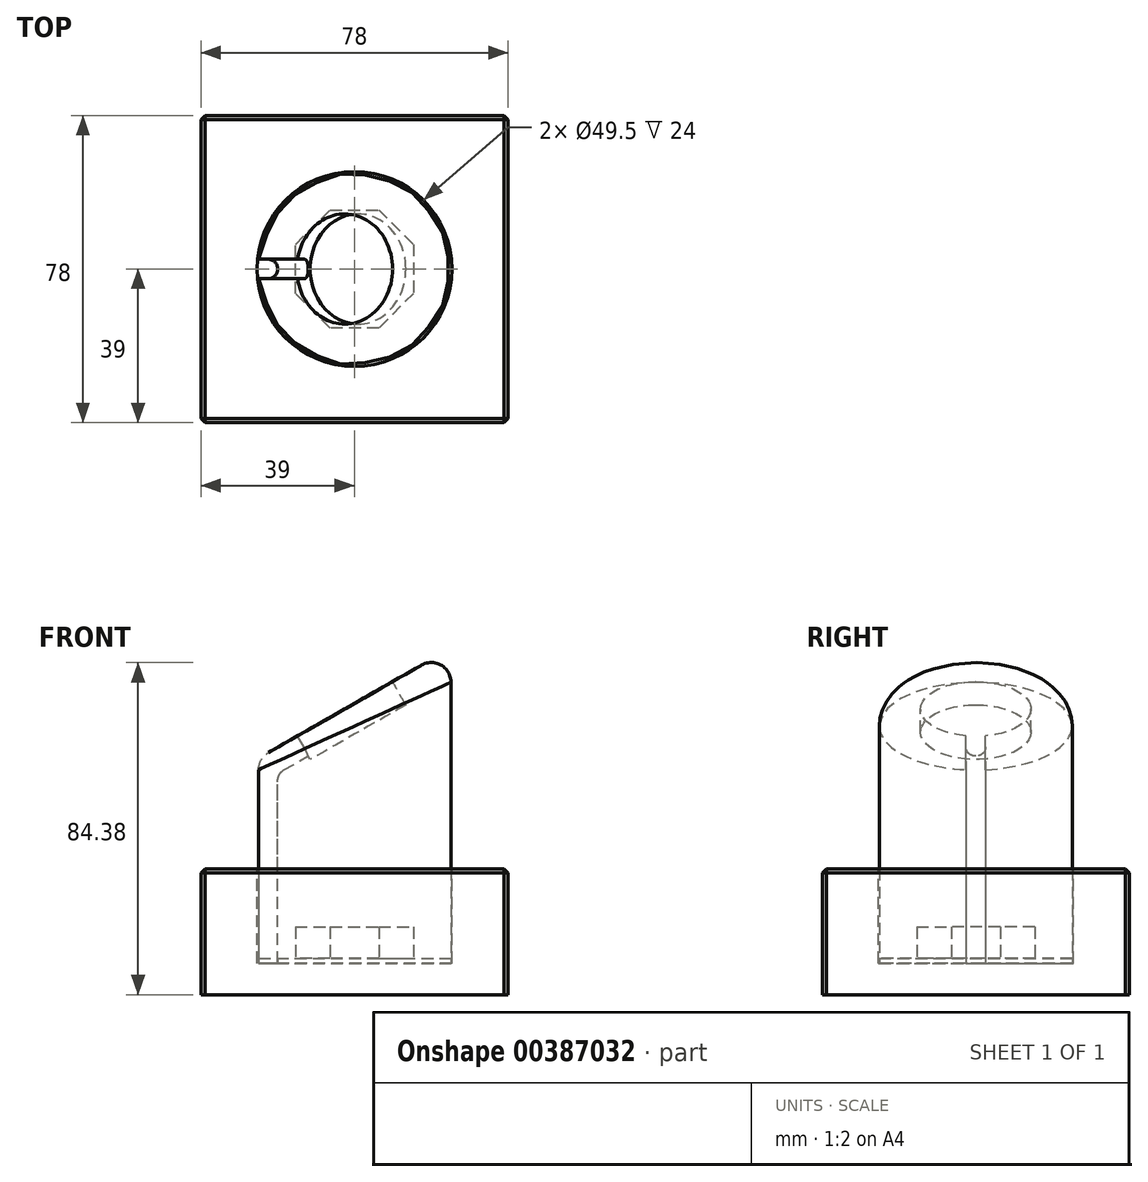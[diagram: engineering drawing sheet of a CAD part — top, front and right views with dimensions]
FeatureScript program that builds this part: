
annotation { "Feature Type Name" : "Feature", "Feature Type Description" : "" }
export const myFeature = defineFeature(function(context is Context, id is Id, definition is map)
    precondition{}
    {
        {
            var Q0;
            Q0=qCreatedBy(makeId("Top.planeOp"),FACE);
            var sketch = newSketch(context, id + "F0", { "sketchPlane" : qUnion([Q0])});
            skLineSegment(sketch, "E0.bottom", {"start": v(39, -39) * mm, "end": v(-39, -39) * mm});
            skLineSegment(sketch, "E0.top", {"start": v(39, 39) * mm, "end": v(-39, 39) * mm});
            skLineSegment(sketch, "E0.left", {"start": v(39, -39) * mm, "end": v(39, 39) * mm});
            skLineSegment(sketch, "E0.right", {"start": v(-39, -39) * mm, "end": v(-39, 39) * mm});
            skPoint(sketch, "E0.middle", {"position": v(0, 0) * mm});
            skSolve(sketch);
        }
        {
            var Q0;
            Q0 = qSketchRegion(id + "F0", true);
            extrude(context, id + "F1", {"entities" : qUnion([Q0]), "depth" : 32 * mm});
        }
        {
            var Q0;
            Q0=makeQuery(id+"F1.opExtrude","CAP_FACE",FACE,{"disambiguationData":[OSD([sQuery(id+"F0.wireOp",EDGE,"E0.bottom"),sQuery(id+"F0.wireOp",EDGE,"E0.top"),sQuery(id+"F0.wireOp",EDGE,"E0.left"),sQuery(id+"F0.wireOp",EDGE,"E0.right")])],"isStart":false});
            var sketch = newSketch(context, id + "F2", { "sketchPlane" : qUnion([Q0])});
            skCircle(sketch, "E1", {"center": v(0, 0) * mm, "radius": 24.75 * mm});
            skSolve(sketch);
        }
        {
            var Q0;
            Q0 = qSketchRegion(id + "F2", true);
            extrude(context, id + "F3", {"entities" : qUnion([Q0]), "operationType" : NewBodyOperationType.REMOVE, "oppositeDirection" : true, "depth" : 24 * mm});
        }
        {
            var Q0;
            Q0=makeQuery(id+"F3.boolean.opBoolean","COPY",FACE,{"derivedFrom":makeQuery(id+"F3.opExtrude","CAP_FACE",FACE,{"disambiguationData":[OSD([sQuery(id+"F2.wireOp",EDGE,"E1")])],"isStart":false})});
            var sketch = newSketch(context, id + "F4", { "sketchPlane" : qUnion([Q0])});
            skCircle(sketch, "E2", {"center": v(0, 0) * mm, "radius": 24.5 * mm});
            skSolve(sketch);
        }
        {
            var Q0;
            Q0 = qSketchRegion(id + "F4", true);
            extrude(context, id + "F5", {"entities" : qUnion([Q0]), "depth" : 1.2 * mm});
        }
        {
            var Q0;
            Q0=makeQuery(id+"F5.opExtrude","CAP_FACE",FACE,{"disambiguationData":[OSD([sQuery(id+"F4.wireOp",EDGE,"E2")])],"isStart":false});
            var sketch = newSketch(context, id + "F6", { "sketchPlane" : qUnion([Q0])});
            skCircle(sketch, "E3.cCircle", {"center": v(0, 0) * mm, "radius": 15 * mm, "construction": true});
            skLineSegment(sketch, "E3.0", {"start": v(15, 6.21) * mm, "end": v(15, -6.21) * mm});
            skLineSegment(sketch, "E3.1", {"start": v(15, -6.21) * mm, "end": v(6.21, -15) * mm});
            skLineSegment(sketch, "E3.2", {"start": v(6.21, -15) * mm, "end": v(-6.21, -15) * mm});
            skLineSegment(sketch, "E3.3", {"start": v(-6.21, -15) * mm, "end": v(-15, -6.21) * mm});
            skLineSegment(sketch, "E3.4", {"start": v(-15, -6.21) * mm, "end": v(-15, 6.21) * mm});
            skLineSegment(sketch, "E3.5", {"start": v(-15, 6.21) * mm, "end": v(-6.21, 15) * mm});
            skLineSegment(sketch, "E3.6", {"start": v(-6.21, 15) * mm, "end": v(6.21, 15) * mm});
            skLineSegment(sketch, "E3.7", {"start": v(6.21, 15) * mm, "end": v(15, 6.21) * mm});
            skPoint(sketch, "E3.0.midPoint", {"position": v(15, 0) * mm});
            skSolve(sketch);
        }
        {
            var Q0;
            Q0 = qSketchRegion(id + "F6", true);
            extrude(context, id + "F7", {"entities" : qUnion([Q0]), "operationType" : NewBodyOperationType.ADD, "depth" : 8 * mm});
        }
        {
            var Q0;
            Q0=makeQuery(id+"F3.boolean.opBoolean","COPY",FACE,{"derivedFrom":makeQuery(id+"F3.opExtrude","CAP_FACE",FACE,{"disambiguationData":[OSD([sQuery(id+"F2.wireOp",EDGE,"E1")])],"isStart":false})});
            var sketch = newSketch(context, id + "F8", { "sketchPlane" : qUnion([Q0])});
            skCircle(sketch, "E4", {"center": v(0, 0) * mm, "radius": 24.5 * mm});
            skSolve(sketch);
        }
        {
            var Q0;
            Q0 = qSketchRegion(id + "F8", true);
            extrude(context, id + "F9", {"entities" : qUnion([Q0]), "depth" : 80 * mm});
        }
        {
            var Q0;
            Q0=qCreatedBy(makeId("Front.planeOp"),FACE);
            var sketch = newSketch(context, id + "F10", { "sketchPlane" : qUnion([Q0])});
            skLineSegment(sketch, "E5.0", {"start": v(-24.5, 88) * mm, "end": v(24.5, 88) * mm});
            skLineSegment(sketch, "E6", {"start": v(24.5, 88) * mm, "end": v(-24.5, 60) * mm});
            skLineSegment(sketch, "E7", {"start": v(-24.5, 60) * mm, "end": v(-24.5, 88) * mm});
            skSolve(sketch);
        }
        {
            var Q0;
            Q0 = qSketchRegion(id + "F10", true);
            extrude(context, id + "F11", {"entities" : qUnion([Q0]), "operationType" : NewBodyOperationType.REMOVE, "oppositeDirection" : true, "depth" : 25 * mm, "hasSecondDirection" : true, "secondDirectionOppositeDirection" : false, "secondDirectionDepth" : 25 * mm});
        }
        {
            var Q0;
            Q0=makeQuery(id+"F11.boolean.opBoolean","INTERSECT",EDGE,{"derivedFrom":[makeQuery(id+"F9.opExtrude","SWEPT_FACE",FACE,{"disambiguationData":[OSD([sQuery(id+"F8.wireOp",EDGE,"E4")])]}),makeQuery(id+"F11.opExtrude","SWEPT_FACE",FACE,{"disambiguationData":[OSD([sQuery(id+"F10.wireOp",EDGE,"E6")])]})]});
            fillet(context, id + "F12", {"entities" : qUnion([Q0]), "radius" : 5 * mm, "tangentPropagation" : true, "allowEdgeOverflow" : false});
        }
        {
            var Q0;
            Q0=makeQuery(id+"F11.boolean.opBoolean","COPY",FACE,{"derivedFrom":makeQuery(id+"F11.opExtrude","SWEPT_FACE",FACE,{"disambiguationData":[OSD([sQuery(id+"F10.wireOp",EDGE,"E6")])]})});
            var sketch = newSketch(context, id + "F13", { "sketchPlane" : qUnion([Q0])});
            skCircle(sketch, "E8", {"center": v(33.86, 0) * mm, "radius": 14 * mm});
            skPoint(sketch, "E9.0", {"position": v(0, 0) * mm});
            skLineSegment(sketch, "E10", {"start": v(33.86, 0) * mm, "end": v(0, 0) * mm});
            skSolve(sketch);
        }
        {
            var Q0;
            Q0 = qSketchRegion(id + "F13", true);
            extrude(context, id + "F14", {"entities" : qUnion([Q0]), "operationType" : NewBodyOperationType.REMOVE, "oppositeDirection" : true, "depth" : 6.8 * mm});
        }
        {
            var Q0;
            Q0=makeQuery(id+"F1.opExtrude","CAP_EDGE",EDGE,{"disambiguationData":[OSD([sQuery(id+"F0.wireOp",EDGE,"E0.right")])],"isStart":false});
            var Q1;
            Q1=makeQuery(id+"F1.opExtrude","CAP_EDGE",EDGE,{"disambiguationData":[OSD([sQuery(id+"F0.wireOp",EDGE,"E0.top")])],"isStart":false});
            var Q2;
            Q2=makeQuery(id+"F1.opExtrude","CAP_EDGE",EDGE,{"disambiguationData":[OSD([sQuery(id+"F0.wireOp",EDGE,"E0.left")])],"isStart":false});
            var Q3;
            Q3=makeQuery(id+"F1.opExtrude","SWEPT_EDGE",EDGE,{"disambiguationData":[OSD([sQuery(id+"F0.wireOp",EDGE,"E0.bottom"),sQuery(id+"F0.wireOp",EDGE,"E0.right")])]});
            var Q4;
            Q4=makeQuery(id+"F1.opExtrude","SWEPT_EDGE",EDGE,{"disambiguationData":[OSD([sQuery(id+"F0.wireOp",EDGE,"E0.bottom"),sQuery(id+"F0.wireOp",EDGE,"E0.left")])]});
            var Q5;
            Q5=makeQuery(id+"F1.opExtrude","CAP_EDGE",EDGE,{"disambiguationData":[OSD([sQuery(id+"F0.wireOp",EDGE,"E0.bottom")])],"isStart":false});
            var Q6;
            Q6=makeQuery(id+"F1.opExtrude","SWEPT_EDGE",EDGE,{"disambiguationData":[OSD([sQuery(id+"F0.wireOp",EDGE,"E0.top"),sQuery(id+"F0.wireOp",EDGE,"E0.right")])]});
            var Q7;
            Q7=makeQuery(id+"F1.opExtrude","SWEPT_EDGE",EDGE,{"disambiguationData":[OSD([sQuery(id+"F0.wireOp",EDGE,"E0.top"),sQuery(id+"F0.wireOp",EDGE,"E0.left")])]});
            chamfer(context, id + "F15", {"entities" : qUnion([Q0, Q1, Q2, Q3, Q4, Q5, Q6, Q7]), "width" : 1 * mm, "tangentPropagation" : true});
        }
        {
            var Q0;
            Q0=qCreatedBy(makeId("Front.planeOp"),FACE);
            var sketch = newSketch(context, id + "F16", { "sketchPlane" : qUnion([Q0])});
            skLineSegment(sketch, "E11.0", {"start": v(-14.64, 65.64) * mm, "end": v(9.67, 79.53) * mm});
            skLineSegment(sketch, "E12.0", {"start": v(-11.26, 59.73) * mm, "end": v(13.05, 73.62) * mm});
            skLineSegment(sketch, "E13", {"start": v(-11.26, 59.73) * mm, "end": v(-14.64, 65.64) * mm});
            skLineSegment(sketch, "E14", {"start": v(-11.76, 60.6) * mm, "end": v(-25.98, 52.47) * mm});
            skLineSegment(sketch, "E15", {"start": v(-25.98, 52.47) * mm, "end": v(-29.03, 57.8) * mm});
            skLineSegment(sketch, "E16", {"start": v(-14.64, 65.64) * mm, "end": v(-31.2, 56.17) * mm});
            skLineSegment(sketch, "E17", {"start": v(-24.5, 8) * mm, "end": v(-24.5, 57.1) * mm});
            skLineSegment(sketch, "E18", {"start": v(-19.5, 58.7) * mm, "end": v(-19.5, 8) * mm});
            skLineSegment(sketch, "E19", {"start": v(-19.5, 8) * mm, "end": v(-24.5, 8) * mm});
            skLineSegment(sketch, "E20", {"start": v(-11.76, 60.6) * mm, "end": v(-5.93, 63.93) * mm});
            skLineSegment(sketch, "E21", {"start": v(-5.93, 63.93) * mm, "end": v(-8.8, 68.97) * mm});
            skSolve(sketch);
        }
        {
            var Q0;
            Q0 = qSketchRegion(id + "F16", true);
            extrude(context, id + "F17", {"entities" : qUnion([Q0]), "operationType" : NewBodyOperationType.REMOVE, "oppositeDirection" : true, "depth" : 2.5 * mm, "hasSecondDirection" : true, "secondDirectionOppositeDirection" : false, "secondDirectionDepth" : 2.5 * mm});
        }
        {
            var Q0;
            Q0=makeQuery(id+"F17.boolean.opBoolean","COPY",EDGE,{"derivedFrom":makeQuery(id+"F17.opExtrude","SWEPT_EDGE",EDGE,{"disambiguationData":[OSD([sQuery(id+"F16.wireOp",EDGE,"E14"),sQuery(id+"F16.wireOp",EDGE,"E18")])]})});
            fillet(context, id + "F18", {"entities" : qUnion([Q0]), "radius" : 3 * mm, "tangentPropagation" : true, "allowEdgeOverflow" : false});
        }
        {
            var Q0;
            Q0=makeQuery(id+"F17.boolean.opBoolean","COPY",EDGE,{"derivedFrom":makeQuery(id+"F17.opExtrude","CAP_EDGE",EDGE,{"disambiguationData":[OSD([sQuery(id+"F16.wireOp",EDGE,"E14"),sQuery(id+"F16.wireOp",EDGE,"E20")])],"isStart":false})});
            var Q1;
            Q1=makeQuery(id+"F17.boolean.opBoolean","COPY",EDGE,{"derivedFrom":makeQuery(id+"F17.opExtrude","CAP_EDGE",EDGE,{"disambiguationData":[OSD([sQuery(id+"F16.wireOp",EDGE,"E14"),sQuery(id+"F16.wireOp",EDGE,"E20")])],"isStart":true})});
            fillet(context, id + "F19", {"entities" : qUnion([Q0, Q1]), "radius" : 2.5 * mm, "tangentPropagation" : true, "allowEdgeOverflow" : false});
        }
    });
